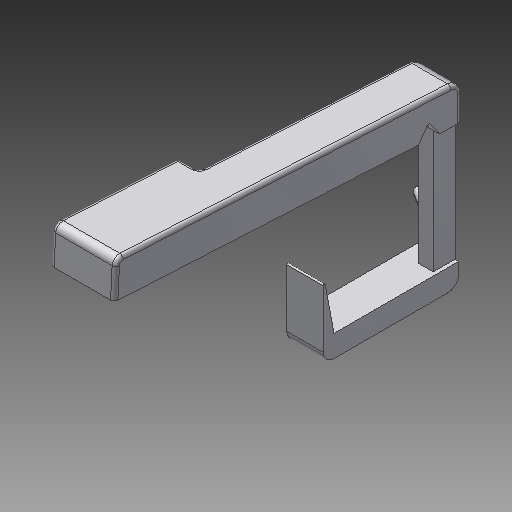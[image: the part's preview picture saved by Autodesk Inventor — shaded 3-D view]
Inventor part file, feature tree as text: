
AUTODESK INVENTOR PART (.ipt)
format: ipt  version: 2018 (Build 220112000, 112)  size: 309,248 bytes
history: native  units: mm
features: extrude x7, fillet x6, other x3, draft x1, chamfer x1
ambient origin geometry x8: Origin, YZ Plane, XZ Plane, XY Plane, X Axis, Y Axis, Z Axis, Center Point
bodies: Solid1 (feature_tree)
feature tree (18):
  other  "Key Sketch"
  extrude  "Upper Key"  Depth=10.0mm
  extrude  "Lower Key"  Depth=1.0mm
  other  "Hinge Cut Sketch"
  extrude  "Hinge Cut"  Depth=10.0mm TaperAngle=0.0deg
  extrude  "Hinge Cut 2"  Depth=3.0mm
  other  "Lever Sketch"
  extrude  "Vertical Lever"  Depth=3.0mm
  extrude  "Horizontal Lever"  Depth=33.6625mm
  extrude  "Spring Hook"  Depth=0.5mm
  draft  "FaceDraft3"
  chamfer  "Chamfer1"  Distance=3.0mm
  fillet  "Fillet9"  Radius=6.0mm
  fillet  "Fillet10"  Radius=4.0mm
  fillet  "Fillet5"  Radius=10.0mm
  fillet  "Fillet4"  [1 undecoded]
  fillet  "Fillet11"  Radius=3.0mm
  fillet  "Fillet14"  Radius=2.3mm
note: 1 required parameter value undecoded (feature->parameter linkage not recoverable at this tier; creation-order binding heuristic only, values carry confidence <= 0.55)
